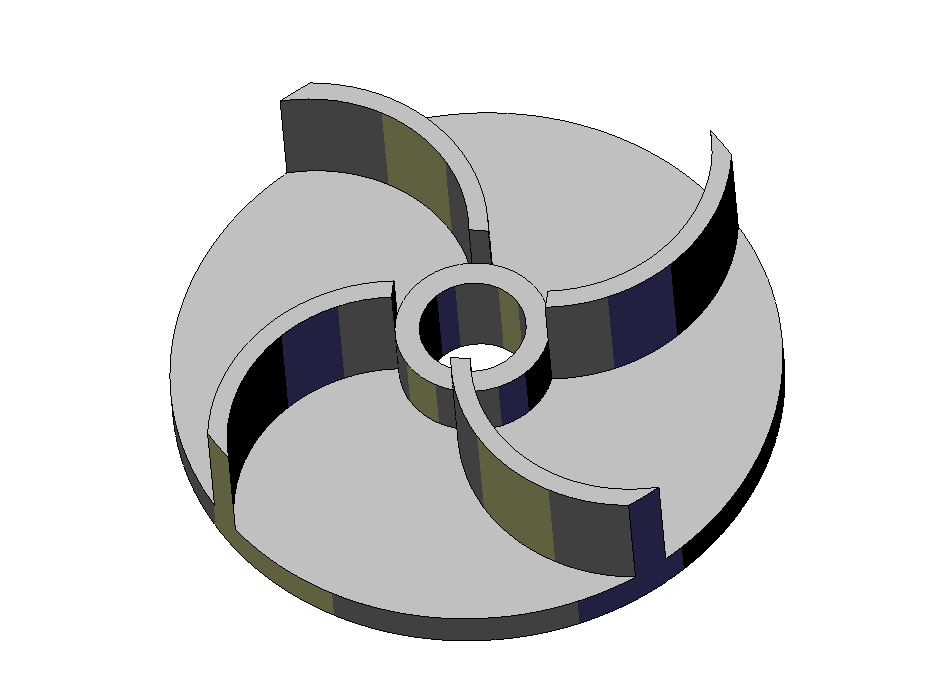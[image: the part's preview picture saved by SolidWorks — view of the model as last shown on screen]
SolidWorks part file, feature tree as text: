
SOLIDWORKS PART (.sldprt)
format: sldprt  version: not decoded by parser v0  size: 316,928 bytes
history: native  units: mm
features: sketch x5, extrude x3, cut_extrude x2, material x1, pattern_circular x1 (+12 scaffold rows collapsed)
feature tree (24):
  scaffold x12  (default folders/planes/origin — collapsed)
  material  "Material <not specified>"
  sketch  "Sketch1"  dims[D1=63.0mm]
  extrude  "Extrude1"  Depth=4mm
  sketch  "Sketch2"  dims[c1.D1=16.0mm c1.D2=70.0mm c1.D3=40.0mm c1.D4=18.0mm c2.D3=20.0mm c2.D2=70.0mm c2.D1=11.0mm c2.D4=12.0mm c2.D5=12.0mm c2.D6=8.0mm c3.D5=35.0mm c3.D2=1.0mm c3.D3=1.0mm]
  extrude  "Extrude3"  Depth=13mm
  sketch  "Sketch3"  dims[D1=16.0mm]
  pattern_circular  "CirPattern1"  Count=4 Angle=360deg
  cut_extrude  "Cut-Extrude1"  Depth=7mm
  sketch  "Sketch4"
  cut_extrude  "Cut-Extrude2"  [1 undecoded]
  sketch  "Sketch5"  dims[D1=16.0mm]
  extrude  "Extrude4"  Depth=7mm
decode coverage: 9 of 11 modeling features carry decoded parameters
note: 1 parameter value undecoded
note: suppression state not decoded; provenance and decode notes live in map.json
